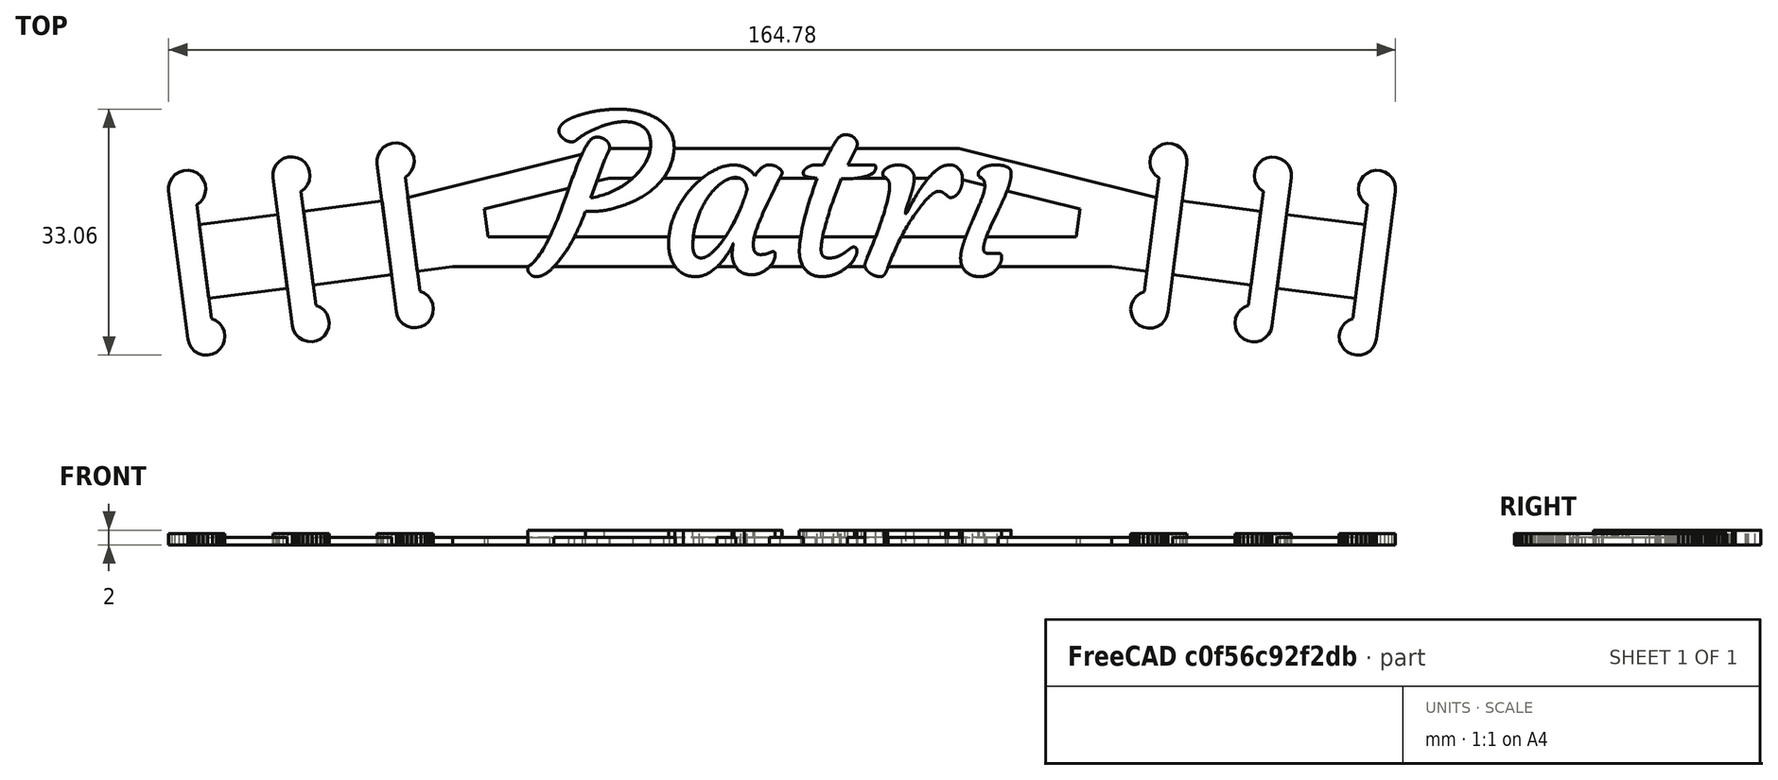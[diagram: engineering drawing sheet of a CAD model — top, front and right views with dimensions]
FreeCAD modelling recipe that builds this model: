
FCSTD DOCUMENT  (FreeCAD 0.18R4 (GitTag))
Label: ear_saver_tito
License: All rights reserved
LicenseURL: http://en.wikipedia.org/wiki/All_rights_reserved
objects: Part::Feature×1, Part::Part2DObjectPython×1, Part::Extrusion×1, Part::Box×1, Part::Cut×1, Part::MultiFuse×1, Mesh::Feature×1
note: 6 computed .brp shape members not serialized (recipe doc carries the construction recipe); baked Part::Feature solids carry a one-line shape summary decoded from their .brp

FEATURE [Part::Feature] ear_saver001_solid001  label="ear_saver001 (Solid)001"
  shape: bbox 164.8 x 28.52 x 1.5 mm, 279 faces (baked)
FEATURE [Part::Part2DObjectPython] ShapeString  # Draft 2D object (typed FeaturePython)
  FontFile = <userpath>/Documents/fonts/Courgette-Regular.ttf
  Placement = pos=(-20.38,14.74,0) rot=(0,0,1;0rad)
  Size = 25
  String = Patri
  Tracking = 0
FEATURE [Part::Extrusion] Extrude001
  Base = -> ShapeString
  Dir = (0,0,1)
  DirMode = 2
  FaceMakerClass = Part::FaceMakerBullseye
  LengthFwd = 2
  LengthRev = 0
  Placement = pos=(-16,-29,0) rot=(0,0,1;0rad)
  Solid = true
  Symmetric = false
FEATURE [Part::Box] Box  label="Cube"
  AttacherType = Attacher::AttachEngine3D
  Height = 10
  Length = 10
  Placement = pos=(24,3,-1) rot=(0,0,1;0rad)
  Width = 10
FEATURE [Part::Cut] Cut
  Base = -> Extrude001
  Tool = -> Box
FEATURE [Part::MultiFuse] Fusion
  Shapes = -> [Cut,ear_saver001_solid001]
FEATURE [Mesh::Feature] Mesh  label="Fusion (Meshed)"
